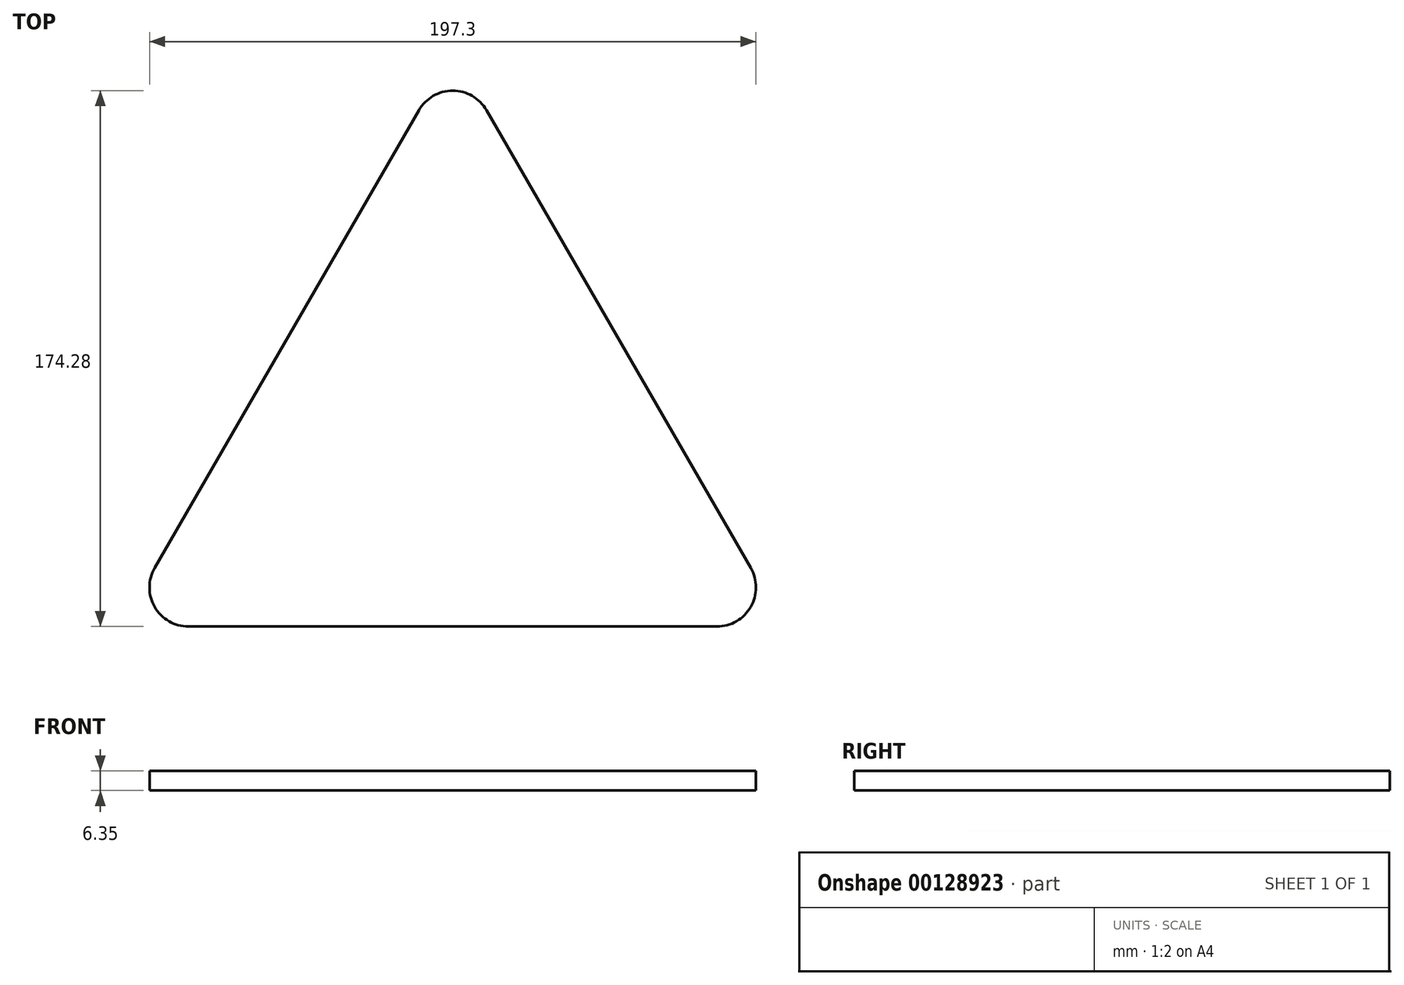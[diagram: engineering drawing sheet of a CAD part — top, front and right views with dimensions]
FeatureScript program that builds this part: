
annotation { "Feature Type Name" : "Feature", "Feature Type Description" : "" }
export const myFeature = defineFeature(function(context is Context, id is Id, definition is map)
    precondition{}
    {
        {
            var Q0;
            Q0=qCreatedBy(makeId("Top.planeOp"),FACE);
            var sketch = newSketch(context, id + "F0", { "sketchPlane" : qUnion([Q0])});
            skLineSegment(sketch, "E0", {"start": v(-85.95, -117.3) * mm, "end": v(85.95, -117.3) * mm});
            skLineSegment(sketch, "E1", {"start": v(-96.95, -98.26) * mm, "end": v(-11, 50.62) * mm});
            skLineSegment(sketch, "E2", {"start": v(11, 50.62) * mm, "end": v(96.95, -98.26) * mm});
            skPoint(sketch, "E3.visualSharp", {"position": v(0, 69.67) * mm});
            skArc(sketch, "E3.filletArc", {"start": v(11, 50.62) * mm, "mid": v(0, 56.97) * mm, "end": v(-11, 50.62) * mm});
            skPoint(sketch, "E4.visualSharp", {"position": v(-107.95, -117.3) * mm});
            skArc(sketch, "E4.filletArc", {"start": v(-96.95, -98.26) * mm, "mid": v(-96.95, -110.96) * mm, "end": v(-85.95, -117.3) * mm});
            skPoint(sketch, "E5.visualSharp", {"position": v(107.95, -117.3) * mm});
            skArc(sketch, "E5.filletArc", {"start": v(85.95, -117.3) * mm, "mid": v(96.95, -110.96) * mm, "end": v(96.95, -98.26) * mm});
            skLineSegment(sketch, "E6", {"start": v(-7.5, 24.77) * mm, "end": v(4.44, 24.77) * mm});
            skSolve(sketch);
        }
        {
            var Q0;
            Q0=makeQuery(id+"F0.imprint","IMPRINT",FACE,{"disambiguationData":[TD([[makeQuery(id+"F0.imprint","IMPRINT",EDGE,{"derivedFrom":sQuery(id+"F0.wireOp",EDGE,"E0")}),1.0]])]});
            extrude(context, id + "F1", {"entities" : qUnion([Q0]), "depth" : 6.35 * mm});
        }
    });
